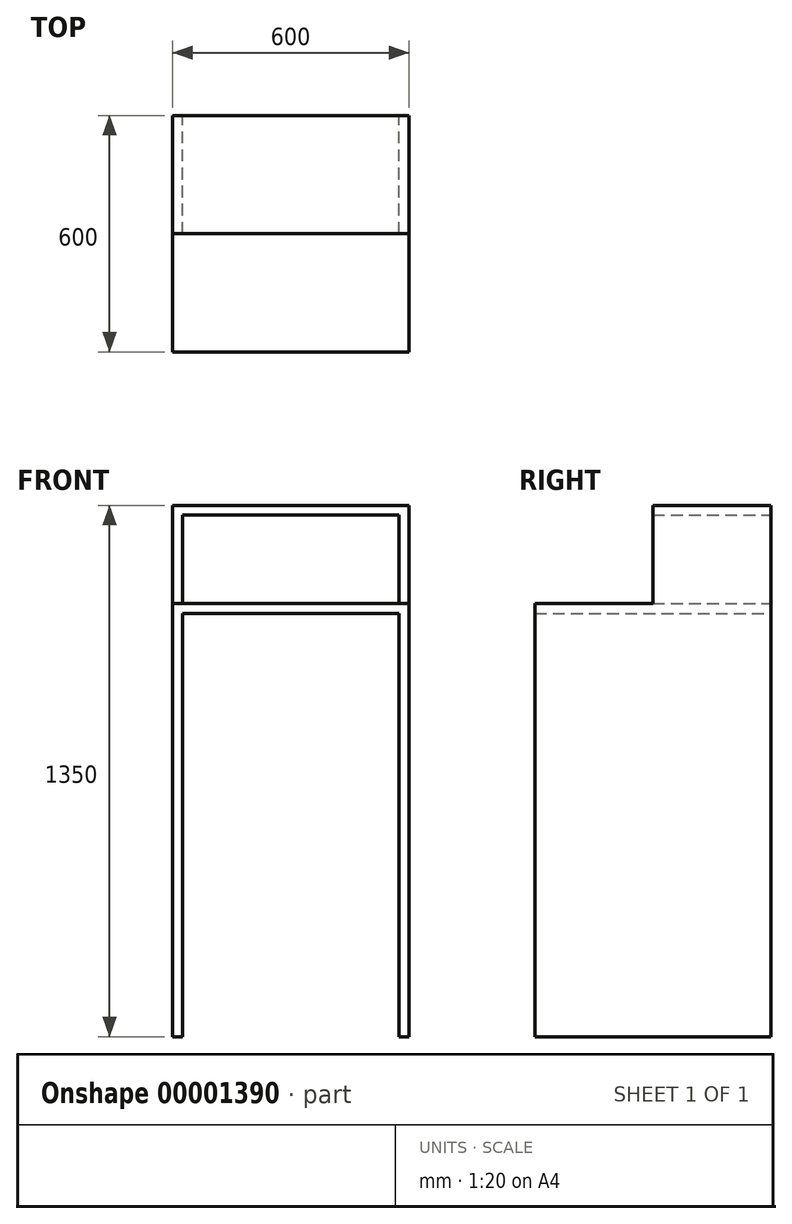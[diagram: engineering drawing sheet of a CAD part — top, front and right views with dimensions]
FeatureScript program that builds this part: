
annotation { "Feature Type Name" : "Feature", "Feature Type Description" : "" }
export const myFeature = defineFeature(function(context is Context, id is Id, definition is map)
    precondition{}
    {
        {
            var Q0;
            Q0=qCreatedBy(makeId("Front.planeOp"),FACE);
            var sketch = newSketch(context, id + "F0", { "sketchPlane" : qUnion([Q0])});
            skLineSegment(sketch, "E0.bottom", {"start": v(-295.86, 0) * mm, "end": v(-270.86, 0) * mm});
            skLineSegment(sketch, "E0.top", {"start": v(-295.86, 1350) * mm, "end": v(304.14, 1350) * mm});
            skLineSegment(sketch, "E0.left", {"start": v(-295.86, 0) * mm, "end": v(-295.86, 1350) * mm});
            skLineSegment(sketch, "E0.right", {"start": v(304.14, 0) * mm, "end": v(304.14, 1350) * mm});
            skLineSegment(sketch, "E1.0", {"start": v(-270.86, 1325) * mm, "end": v(279.14, 1325) * mm});
            skLineSegment(sketch, "E2.0", {"start": v(279.14, 0) * mm, "end": v(279.14, 1325) * mm});
            skLineSegment(sketch, "E3.0", {"start": v(-270.86, 0) * mm, "end": v(-270.86, 1325) * mm});
            skLineSegment(sketch, "E4.trimOffspring", {"start": v(279.14, 0) * mm, "end": v(304.14, 0) * mm});
            skLineSegment(sketch, "E5", {"start": v(4.14, 1350) * mm, "end": v(0, 0) * mm, "construction": true});
            skSolve(sketch);
        }
        {
            var Q0;
            Q0 = qSketchRegion(id + "F0", true);
            extrude(context, id + "F1", {"entities" : qUnion([Q0]), "depth" : 300 * mm});
        }
        {
            var Q0;
            Q0=qCreatedBy(makeId("Front.planeOp"),FACE);
            var sketch = newSketch(context, id + "F2", { "sketchPlane" : qUnion([Q0])});
            skLineSegment(sketch, "E6.0", {"start": v(-295.86, 1075) * mm, "end": v(-295.86, 1100) * mm});
            skLineSegment(sketch, "E7.0", {"start": v(304.14, 1075) * mm, "end": v(304.14, 1100) * mm});
            skLineSegment(sketch, "E8.bottom", {"start": v(-295.86, 1100) * mm, "end": v(304.14, 1100) * mm});
            skLineSegment(sketch, "E8.top", {"start": v(-295.86, 1075) * mm, "end": v(304.14, 1075) * mm});
            skLineSegment(sketch, "E8.left", {"start": v(-295.86, 1100) * mm, "end": v(-295.86, 1075) * mm});
            skLineSegment(sketch, "E8.right", {"start": v(304.14, 1100) * mm, "end": v(304.14, 1075) * mm});
            skPoint(sketch, "E9.orphan", {"position": v(304.14, 1350) * mm});
            skPoint(sketch, "E10.orphan", {"position": v(304.14, 0) * mm});
            skPoint(sketch, "E11.orphan", {"position": v(-295.86, 1350) * mm});
            skPoint(sketch, "E12.orphan", {"position": v(-295.86, 0) * mm});
            skSolve(sketch);
        }
        {
            var Q0;
            Q0 = qSketchRegion(id + "F2", true);
            extrude(context, id + "F3", {"entities" : qUnion([Q0]), "operationType" : NewBodyOperationType.ADD, "depth" : 600 * mm});
        }
        {
            var Q0;
            {var subQ0=sQuery(id+"F0.wireOp",EDGE,"E0.bottom");var subQ1=sQuery(id+"F0.wireOp",EDGE,"E0.left");var subQ2=sQuery(id+"F0.wireOp",EDGE,"E3.0");Q0=makeQuery(id+"F3.boolean.opBoolean","SPLIT",FACE,{"disambiguationData":[TD([makeQuery(id+"F1.opExtrude","SWEPT_FACE",FACE,{"disambiguationData":[OSD([subQ0])]})])],"derivedFrom":makeQuery(id+"F1.opExtrude","CAP_FACE",FACE,{"disambiguationData":[OSD([subQ0,sQuery(id+"F0.wireOp",EDGE,"E0.top"),subQ1,sQuery(id+"F0.wireOp",EDGE,"E0.right"),sQuery(id+"F0.wireOp",EDGE,"E1.0"),sQuery(id+"F0.wireOp",EDGE,"E2.0"),subQ2,sQuery(id+"F0.wireOp",EDGE,"E4.trimOffspring")])],"isStart":false})});}
            var Q1;
            {var subQ0=sQuery(id+"F0.wireOp",EDGE,"E0.right");var subQ1=sQuery(id+"F0.wireOp",EDGE,"E2.0");var subQ2=sQuery(id+"F0.wireOp",EDGE,"E4.trimOffspring");Q1=makeQuery(id+"F3.boolean.opBoolean","SPLIT",FACE,{"disambiguationData":[TD([makeQuery(id+"F1.opExtrude","SWEPT_FACE",FACE,{"disambiguationData":[OSD([subQ2])]})])],"derivedFrom":makeQuery(id+"F1.opExtrude","CAP_FACE",FACE,{"disambiguationData":[OSD([sQuery(id+"F0.wireOp",EDGE,"E0.bottom"),sQuery(id+"F0.wireOp",EDGE,"E0.top"),sQuery(id+"F0.wireOp",EDGE,"E0.left"),subQ0,sQuery(id+"F0.wireOp",EDGE,"E1.0"),subQ1,sQuery(id+"F0.wireOp",EDGE,"E3.0"),subQ2])],"isStart":false})});}
            var Q2;
            Q2=makeQuery(id+"F3.opExtrude","CAP_FACE",FACE,{"disambiguationData":[OSD([sQuery(id+"F2.wireOp",EDGE,"E8.bottom"),sQuery(id+"F2.wireOp",EDGE,"E8.top"),sQuery(id+"F2.wireOp",EDGE,"E8.left"),sQuery(id+"F2.wireOp",EDGE,"E8.right")])],"isStart":false});
            extrude(context, id + "F4", {"entities" : qUnion([Q0, Q1]), "operationType" : NewBodyOperationType.ADD, "endBound" : BoundingType.UP_TO_SURFACE, "endBoundEntityFace" : qUnion([Q2]), "depth" : 25 * mm});
        }
    });
